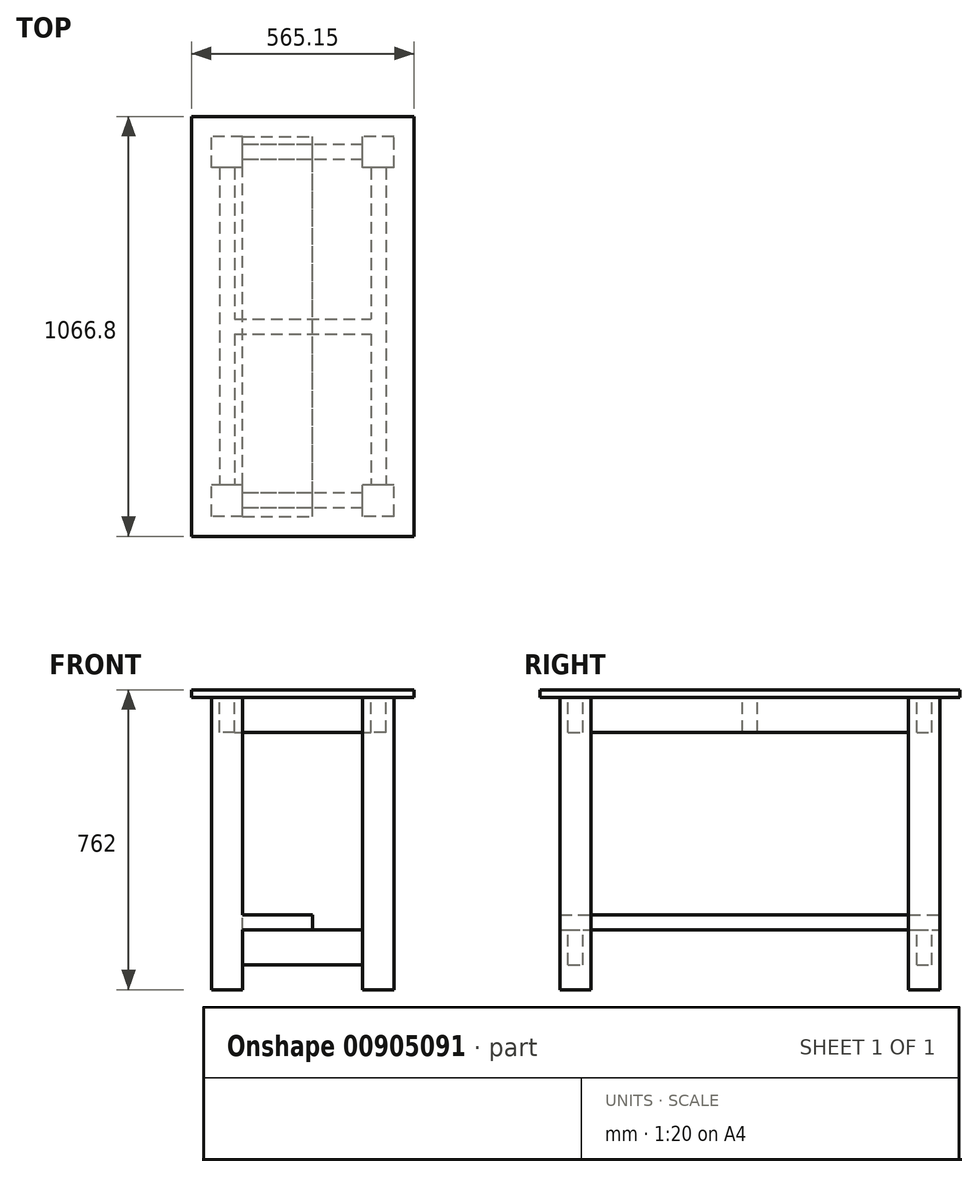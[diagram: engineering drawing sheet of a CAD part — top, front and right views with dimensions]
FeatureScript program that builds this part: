
annotation { "Feature Type Name" : "Feature", "Feature Type Description" : "" }
export const myFeature = defineFeature(function(context is Context, id is Id, definition is map)
    precondition{}
    {
        {
            var Q0;
            Q0=qCreatedBy(makeId("Top.planeOp"),FACE);
            var sketch = newSketch(context, id + "F0", { "sketchPlane" : qUnion([Q0])});
            skLineSegment(sketch, "E0.bottom", {"start": v(0, 0) * mm, "end": v(565.15, 0) * mm});
            skLineSegment(sketch, "E0.top", {"start": v(0, 1066.8) * mm, "end": v(565.15, 1066.8) * mm});
            skLineSegment(sketch, "E0.left", {"start": v(0, 0) * mm, "end": v(0, 1066.8) * mm});
            skLineSegment(sketch, "E0.right", {"start": v(565.15, 0) * mm, "end": v(565.15, 1066.8) * mm});
            skSolve(sketch);
        }
        {
            var Q0;
            Q0=makeQuery(id+"F0.imprint","IMPRINT",FACE,{"disambiguationData":[TD([[makeQuery(id+"F0.imprint","IMPRINT",EDGE,{"derivedFrom":sQuery(id+"F0.wireOp",EDGE,"E0.bottom")}),1.0]])]});
            extrude(context, id + "F1", {"entities" : qUnion([Q0]), "depth" : 19.05 * mm, "offsetDistance" : 25.4 * mm});
        }
        {
            var Q0;
            Q0=makeQuery(id+"F1.opExtrude","CAP_FACE",FACE,{"disambiguationData":[OSD([sQuery(id+"F0.wireOp",EDGE,"E0.bottom"),sQuery(id+"F0.wireOp",EDGE,"E0.top"),sQuery(id+"F0.wireOp",EDGE,"E0.left"),sQuery(id+"F0.wireOp",EDGE,"E0.right")])],"isStart":true});
            var sketch = newSketch(context, id + "F2", { "sketchPlane" : qUnion([Q0])});
            skLineSegment(sketch, "E1.bottom", {"start": v(130.18, -50.8) * mm, "end": v(50.8, -50.8) * mm});
            skLineSegment(sketch, "E1.top", {"start": v(130.18, -130.18) * mm, "end": v(50.8, -130.18) * mm});
            skLineSegment(sketch, "E1.left", {"start": v(130.18, -50.8) * mm, "end": v(130.18, -130.18) * mm});
            skLineSegment(sketch, "E1.right", {"start": v(50.8, -50.8) * mm, "end": v(50.8, -130.18) * mm});
            skLineSegment(sketch, "E2.bottom", {"start": v(514.35, -50.8) * mm, "end": v(434.98, -50.8) * mm});
            skLineSegment(sketch, "E2.top", {"start": v(514.35, -130.18) * mm, "end": v(434.98, -130.18) * mm});
            skLineSegment(sketch, "E2.left", {"start": v(514.35, -50.8) * mm, "end": v(514.35, -130.18) * mm});
            skLineSegment(sketch, "E2.right", {"start": v(434.98, -50.8) * mm, "end": v(434.98, -130.18) * mm});
            skLineSegment(sketch, "E3.bottom", {"start": v(514.35, -936.63) * mm, "end": v(434.97, -936.63) * mm});
            skLineSegment(sketch, "E3.top", {"start": v(514.35, -1016) * mm, "end": v(434.97, -1016) * mm});
            skLineSegment(sketch, "E3.left", {"start": v(514.35, -936.63) * mm, "end": v(514.35, -1016) * mm});
            skLineSegment(sketch, "E3.right", {"start": v(434.97, -936.63) * mm, "end": v(434.97, -1016) * mm});
            skLineSegment(sketch, "E4.bottom", {"start": v(130.18, -936.63) * mm, "end": v(50.8, -936.63) * mm});
            skLineSegment(sketch, "E4.top", {"start": v(130.18, -1016) * mm, "end": v(50.8, -1016) * mm});
            skLineSegment(sketch, "E4.left", {"start": v(130.18, -936.63) * mm, "end": v(130.18, -1016) * mm});
            skLineSegment(sketch, "E4.right", {"start": v(50.8, -936.63) * mm, "end": v(50.8, -1016) * mm});
            skLineSegment(sketch, "E5", {"start": v(434.97, -976.31) * mm, "end": v(130.18, -976.31) * mm});
            skLineSegment(sketch, "E6.0", {"start": v(434.98, -71.44) * mm, "end": v(130.18, -71.44) * mm});
            skLineSegment(sketch, "E7.0", {"start": v(-6.35, -1073.15) * mm, "end": v(571.5, -1073.15) * mm});
            skLineSegment(sketch, "E7.1", {"start": v(-6.35, 6.35) * mm, "end": v(-6.35, -1073.15) * mm});
            skLineSegment(sketch, "E7.2", {"start": v(571.5, 6.35) * mm, "end": v(-6.35, 6.35) * mm});
            skLineSegment(sketch, "E7.3", {"start": v(571.5, -1073.15) * mm, "end": v(571.5, 6.35) * mm});
            skLineSegment(sketch, "E8.0", {"start": v(434.98, -109.54) * mm, "end": v(130.18, -109.54) * mm});
            skSolve(sketch);
        }
        {
            var Q0;
            Q0=makeQuery(id+"F2.imprint","IMPRINT",FACE,{"disambiguationData":[TD([[makeQuery(id+"F2.imprint","IMPRINT",EDGE,{"derivedFrom":sQuery(id+"F2.wireOp",EDGE,"E4.bottom")}),1.0]])]});
            var Q1;
            Q1=makeQuery(id+"F2.imprint","IMPRINT",FACE,{"disambiguationData":[TD([[makeQuery(id+"F2.imprint","IMPRINT",EDGE,{"derivedFrom":sQuery(id+"F2.wireOp",EDGE,"E3.bottom")}),1.0]])]});
            var Q2;
            Q2=makeQuery(id+"F2.imprint","IMPRINT",FACE,{"disambiguationData":[TD([[makeQuery(id+"F2.imprint","IMPRINT",EDGE,{"derivedFrom":sQuery(id+"F2.wireOp",EDGE,"E2.bottom")}),1.0]])]});
            var Q3;
            Q3=makeQuery(id+"F2.imprint","IMPRINT",FACE,{"disambiguationData":[TD([[makeQuery(id+"F2.imprint","IMPRINT",EDGE,{"derivedFrom":sQuery(id+"F2.wireOp",EDGE,"E1.bottom")}),1.0]])]});
            extrude(context, id + "F3", {"entities" : qUnion([Q0, Q1, Q2, Q3]), "operationType" : NewBodyOperationType.ADD, "depth" : 742.95 * mm, "offsetDistance" : 25.4 * mm});
        }
        {
            var Q0;
            Q0=makeQuery(id+"F1.opExtrude","CAP_FACE",FACE,{"disambiguationData":[OSD([sQuery(id+"F0.wireOp",EDGE,"E0.bottom"),sQuery(id+"F0.wireOp",EDGE,"E0.top"),sQuery(id+"F0.wireOp",EDGE,"E0.left"),sQuery(id+"F0.wireOp",EDGE,"E0.right")])],"isStart":true});
            var sketch = newSketch(context, id + "F4", { "sketchPlane" : qUnion([Q0])});
            skLineSegment(sketch, "E9", {"start": v(565.15, 0) * mm, "end": v(50.8, 0) * mm});
            skLineSegment(sketch, "E10.0", {"start": v(565.15, -19.05) * mm, "end": v(50.8, -19.05) * mm});
            skLineSegment(sketch, "E11", {"start": v(565.15, -19.05) * mm, "end": v(565.15, 0) * mm});
            skLineSegment(sketch, "E12", {"start": v(50.8, -19.05) * mm, "end": v(50.8, 0) * mm});
            skLineSegment(sketch, "E13.0", {"start": v(565.15, -400.05) * mm, "end": v(50.8, -400.05) * mm});
            skLineSegment(sketch, "E14.0", {"start": v(-6.35, -1073.15) * mm, "end": v(571.5, -1073.15) * mm});
            skLineSegment(sketch, "E14.1", {"start": v(-6.35, 6.35) * mm, "end": v(-6.35, -1073.15) * mm});
            skLineSegment(sketch, "E14.2", {"start": v(571.5, 6.35) * mm, "end": v(-6.35, 6.35) * mm});
            skLineSegment(sketch, "E14.3", {"start": v(571.5, -1073.15) * mm, "end": v(571.5, 6.35) * mm});
            skLineSegment(sketch, "E15.0", {"start": v(565.15, -419.1) * mm, "end": v(50.8, -419.1) * mm});
            skLineSegment(sketch, "E16", {"start": v(50.8, -400.05) * mm, "end": v(50.8, -419.1) * mm});
            skLineSegment(sketch, "E17", {"start": v(565.15, -400.05) * mm, "end": v(565.15, -419.1) * mm});
            skSolve(sketch);
        }
        {
            var Q0;
            {var subQ4=sQuery(id+"F4.wireOp",EDGE,"E10.0");Q0=makeQuery(id+"F4.imprint","IMPRINT",FACE,{"disambiguationData":[TD([[makeQuery(id+"F4.imprint","IMPRINT",EDGE,{"derivedFrom":subQ4}),1.0]])]});}
            var sketch = newSketch(context, id + "F5", { "sketchPlane" : qUnion([Q0])});
            skLineSegment(sketch, "E18.0", {"start": v(434.98, -71.44) * mm, "end": v(434.98, -109.54) * mm});
            skLineSegment(sketch, "E19.0", {"start": v(130.18, -71.44) * mm, "end": v(130.18, -109.54) * mm});
            skLineSegment(sketch, "E20.0", {"start": v(130.18, -957.26) * mm, "end": v(130.18, -995.36) * mm});
            skLineSegment(sketch, "E21.0", {"start": v(434.97, -957.26) * mm, "end": v(434.97, -995.36) * mm});
            skLineSegment(sketch, "E22.0", {"start": v(434.98, -71.44) * mm, "end": v(130.18, -71.44) * mm});
            skLineSegment(sketch, "E23.0", {"start": v(434.98, -109.54) * mm, "end": v(130.18, -109.54) * mm});
            skPoint(sketch, "E24.orphan", {"position": v(434.98, -130.18) * mm});
            skPoint(sketch, "E25.orphan", {"position": v(434.98, -50.8) * mm});
            skPoint(sketch, "E26.orphan", {"position": v(130.18, -50.8) * mm});
            skPoint(sketch, "E27.orphan", {"position": v(130.18, -130.18) * mm});
            skLineSegment(sketch, "E28.0", {"start": v(434.97, -995.36) * mm, "end": v(130.18, -995.36) * mm});
            skLineSegment(sketch, "E29.0", {"start": v(434.97, -957.26) * mm, "end": v(130.18, -957.26) * mm});
            skPoint(sketch, "E30.orphan", {"position": v(130.18, -936.63) * mm});
            skPoint(sketch, "E31.orphan", {"position": v(130.18, -1016) * mm});
            skPoint(sketch, "E32.end.orphan", {"position": v(130.18, -976.31) * mm});
            skPoint(sketch, "E32.start.orphan", {"position": v(434.97, -976.31) * mm});
            skPoint(sketch, "E33.orphan", {"position": v(434.97, -936.63) * mm});
            skPoint(sketch, "E34.orphan", {"position": v(434.97, -1016) * mm});
            skSolve(sketch);
        }
        {
            var Q0;
            Q0 = qSketchRegion(id + "F5", true);
            extrude(context, id + "F6", {"entities" : qUnion([Q0]), "operationType" : NewBodyOperationType.ADD, "depth" : 88.9 * mm, "offsetDistance" : 25.4 * mm});
        }
        {
            var Q0;
            {var subQ4=sQuery(id+"F4.wireOp",EDGE,"E10.0");Q0=makeQuery(id+"F4.imprint","IMPRINT",FACE,{"disambiguationData":[TD([[makeQuery(id+"F4.imprint","IMPRINT",EDGE,{"derivedFrom":subQ4}),1.0]])]});}
            var sketch = newSketch(context, id + "F7", { "sketchPlane" : qUnion([Q0])});
            skLineSegment(sketch, "E35.0", {"start": v(493.71, -936.63) * mm, "end": v(455.61, -936.63) * mm});
            skLineSegment(sketch, "E36.0", {"start": v(109.54, -936.63) * mm, "end": v(71.44, -936.63) * mm});
            skLineSegment(sketch, "E37.0", {"start": v(109.54, -130.18) * mm, "end": v(71.44, -130.18) * mm});
            skLineSegment(sketch, "E38.0", {"start": v(493.71, -130.18) * mm, "end": v(455.61, -130.18) * mm});
            skLineSegment(sketch, "E39.0", {"start": v(455.61, -936.63) * mm, "end": v(455.61, -130.18) * mm});
            skLineSegment(sketch, "E40.0", {"start": v(493.71, -936.63) * mm, "end": v(493.71, -130.18) * mm});
            skLineSegment(sketch, "E41.0", {"start": v(109.54, -936.63) * mm, "end": v(109.54, -130.18) * mm});
            skLineSegment(sketch, "E42.0", {"start": v(71.44, -936.63) * mm, "end": v(71.44, -130.18) * mm});
            skPoint(sketch, "E43.orphan", {"position": v(514.35, -936.63) * mm});
            skPoint(sketch, "E44.orphan", {"position": v(434.97, -936.63) * mm});
            skPoint(sketch, "E45.orphan", {"position": v(130.18, -936.63) * mm});
            skPoint(sketch, "E46.orphan", {"position": v(50.8, -936.63) * mm});
            skPoint(sketch, "E47.orphan", {"position": v(514.35, -130.18) * mm});
            skPoint(sketch, "E48.orphan", {"position": v(434.98, -130.18) * mm});
            skPoint(sketch, "E49.orphan", {"position": v(130.18, -130.18) * mm});
            skPoint(sketch, "E50.orphan", {"position": v(50.8, -130.18) * mm});
            skSolve(sketch);
        }
        {
            var Q0;
            Q0 = qSketchRegion(id + "F7", true);
            extrude(context, id + "F8", {"entities" : qUnion([Q0]), "operationType" : NewBodyOperationType.ADD, "depth" : 88.9 * mm, "offsetDistance" : 25.4 * mm});
        }
        {
            var Q0;
            {var subQ4=sQuery(id+"F4.wireOp",EDGE,"E10.0");Q0=makeQuery(id+"F4.imprint","IMPRINT",FACE,{"disambiguationData":[TD([[makeQuery(id+"F4.imprint","IMPRINT",EDGE,{"derivedFrom":subQ4}),1.0]])]});}
            var sketch = newSketch(context, id + "F9", { "sketchPlane" : qUnion([Q0])});
            skLineSegment(sketch, "E51.0", {"start": v(109.54, -552.45) * mm, "end": v(109.54, -514.35) * mm});
            skLineSegment(sketch, "E52.0", {"start": v(455.61, -552.45) * mm, "end": v(455.61, -514.35) * mm});
            skLineSegment(sketch, "E53.0", {"start": v(109.54, -514.35) * mm, "end": v(455.61, -514.35) * mm});
            skLineSegment(sketch, "E54.0", {"start": v(109.54, -552.45) * mm, "end": v(455.61, -552.45) * mm});
            skPoint(sketch, "E55.orphan", {"position": v(455.61, -936.63) * mm});
            skPoint(sketch, "E56.orphan", {"position": v(455.61, -130.18) * mm});
            skPoint(sketch, "E57.orphan", {"position": v(109.54, -130.18) * mm});
            skPoint(sketch, "E58.orphan", {"position": v(109.54, -936.63) * mm});
            skSolve(sketch);
        }
        {
            var Q0;
            Q0 = qSketchRegion(id + "F9", true);
            extrude(context, id + "F10", {"entities" : qUnion([Q0]), "operationType" : NewBodyOperationType.ADD, "depth" : 88.9 * mm, "offsetDistance" : 25.4 * mm});
        }
        {
            var Q0;
            Q0=makeQuery(id+"F3.opExtrude","CAP_FACE",FACE,{"disambiguationData":[OSD([sQuery(id+"F2.wireOp",EDGE,"E1.bottom"),sQuery(id+"F2.wireOp",EDGE,"E1.top"),sQuery(id+"F2.wireOp",EDGE,"E1.left"),sQuery(id+"F2.wireOp",EDGE,"E1.right")])],"isStart":false});
            cPlane(context, id + "F11", {"entities" : qUnion([Q0]), "cplaneType" : CPlaneType.OFFSET, "offset" : 152.4 * mm, "oppositeDirection" : true, "width" : 152.4 * mm, "height" : 152.4 * mm});
        }
        {
            var Q0;
            Q0=qCreatedBy(id+"F11.planeOp",FACE);
            var sketch = newSketch(context, id + "F12", { "sketchPlane" : qUnion([Q0])});
            skLineSegment(sketch, "E59.0", {"start": v(130.18, -71.44) * mm, "end": v(130.18, -109.54) * mm});
            skLineSegment(sketch, "E60.0", {"start": v(434.98, -71.44) * mm, "end": v(434.98, -109.54) * mm});
            skLineSegment(sketch, "E61.0", {"start": v(434.97, -957.26) * mm, "end": v(434.97, -995.36) * mm});
            skLineSegment(sketch, "E62.0", {"start": v(130.18, -957.26) * mm, "end": v(130.18, -995.36) * mm});
            skLineSegment(sketch, "E63.0", {"start": v(434.98, -71.44) * mm, "end": v(130.18, -71.44) * mm});
            skLineSegment(sketch, "E64.0", {"start": v(434.98, -109.54) * mm, "end": v(130.18, -109.54) * mm});
            skLineSegment(sketch, "E65.0", {"start": v(434.97, -957.26) * mm, "end": v(130.18, -957.26) * mm});
            skLineSegment(sketch, "E66.0", {"start": v(434.97, -995.36) * mm, "end": v(130.18, -995.36) * mm});
            skPoint(sketch, "E67.orphan", {"position": v(434.98, -130.18) * mm});
            skPoint(sketch, "E68.orphan", {"position": v(434.98, -50.8) * mm});
            skPoint(sketch, "E69.orphan", {"position": v(130.18, -50.8) * mm});
            skPoint(sketch, "E70.orphan", {"position": v(130.18, -130.18) * mm});
            skPoint(sketch, "E71.orphan", {"position": v(434.97, -936.63) * mm});
            skPoint(sketch, "E72.orphan", {"position": v(434.97, -1016) * mm});
            skPoint(sketch, "E73.orphan", {"position": v(130.18, -936.63) * mm});
            skPoint(sketch, "E74.orphan", {"position": v(130.18, -1016) * mm});
            skSolve(sketch);
        }
        {
            var Q0;
            Q0 = qSketchRegion(id + "F12", true);
            extrude(context, id + "F13", {"entities" : qUnion([Q0]), "operationType" : NewBodyOperationType.ADD, "depth" : 88.9 * mm, "offsetDistance" : 25.4 * mm});
        }
        {
            var Q0;
            Q0=qCreatedBy(id+"F11.planeOp",FACE);
            var sketch = newSketch(context, id + "F14", { "sketchPlane" : qUnion([Q0])});
            skLineSegment(sketch, "E75", {"start": v(130.18, -1016) * mm, "end": v(307.97, -1016) * mm});
            skLineSegment(sketch, "E76", {"start": v(130.18, -50.8) * mm, "end": v(307.98, -50.8) * mm});
            skLineSegment(sketch, "E77", {"start": v(130.18, -50.8) * mm, "end": v(130.18, -1016) * mm});
            skLineSegment(sketch, "E78.0", {"start": v(307.98, -50.8) * mm, "end": v(307.97, -1016) * mm});
            skPoint(sketch, "E79.orphan", {"position": v(434.98, -50.8) * mm});
            skPoint(sketch, "E80.orphan", {"position": v(434.97, -1016) * mm});
            skSolve(sketch);
        }
        {
            var Q0;
            Q0 = qSketchRegion(id + "F14", true);
            extrude(context, id + "F15", {"entities" : qUnion([Q0]), "operationType" : NewBodyOperationType.ADD, "oppositeDirection" : true, "depth" : 38.1 * mm, "offsetDistance" : 25.4 * mm});
        }
    });
